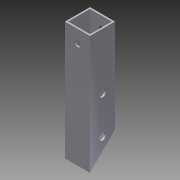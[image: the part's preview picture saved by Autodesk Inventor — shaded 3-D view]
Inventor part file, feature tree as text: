
AUTODESK INVENTOR PART (.ipt)
format: ipt  version: 2013 (Build 170138000, 138)  size: 102,912 bytes
history: native  units: in
note: dims shown in document units (in); Inventor stores cm internally (conversion verified against a paired STEP export)
features: extrude x4, sketch x4, reference x4
ambient origin geometry x8: Origin, YZ Plane, XZ Plane, XY Plane, X Axis, Y Axis, Z Axis, Center Point
bodies: Solid1 (feature_tree)
feature tree (12):
  extrude  "Extrusion1"  Depth=1.0in
  extrude  "Extrusion2"  Depth=4.75in TaperAngle=0.0deg
  extrude  "Extrusion3"  Depth=1.0in TaperAngle=0.0deg
  extrude  "Extrusion4"  Depth=1.0in TaperAngle=0.0deg
  sketch  "Sketch1"  dims[d0=1.0in d2=1.0in]
  sketch  "Sketch2"  dims[d3=0.0625in d4=4.75in d5=0.0in]
  sketch  "Sketch3"  dims[d6=45.0deg d7=1.0in d8=0.0in]
  reference  "Reference1"
  reference  "Reference2"
  sketch  "Sketch4"  dims[d9=1.0in d10=0.0in d11=1.0in d12=0.0in]
  reference  "Reference3"
  reference  "Reference4"
